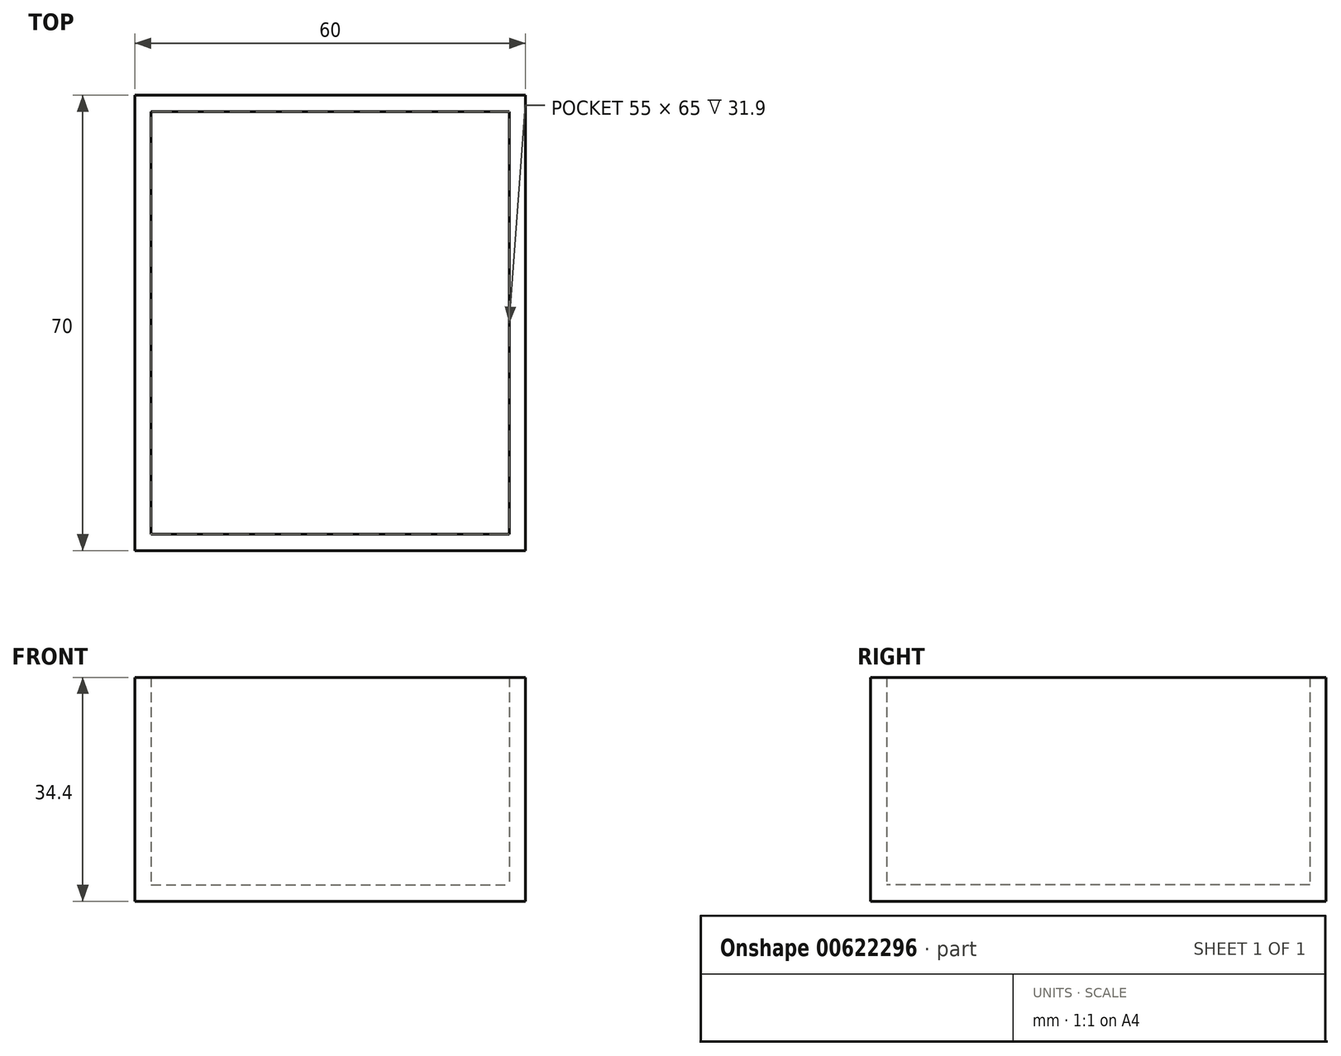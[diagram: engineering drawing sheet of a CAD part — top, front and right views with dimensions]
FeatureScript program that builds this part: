
annotation { "Feature Type Name" : "Feature", "Feature Type Description" : "" }
export const myFeature = defineFeature(function(context is Context, id is Id, definition is map)
    precondition{}
    {
        {
            var Q0;
            Q0=qCreatedBy(makeId("Top.planeOp"),FACE);
            var sketch = newSketch(context, id + "F0", { "sketchPlane" : qUnion([Q0])});
            skLineSegment(sketch, "E0.bottom", {"start": v(-30, 49.8) * mm, "end": v(30, 49.8) * mm});
            skLineSegment(sketch, "E0.top", {"start": v(-30, -20.2) * mm, "end": v(30, -20.2) * mm});
            skLineSegment(sketch, "E0.left", {"start": v(-30, 49.8) * mm, "end": v(-30, -20.2) * mm});
            skLineSegment(sketch, "E0.right", {"start": v(30, 49.8) * mm, "end": v(30, -20.2) * mm});
            skPoint(sketch, "E1", {"position": v(0, 49.8) * mm});
            skSolve(sketch);
        }
        {
            var Q0;
            Q0 = qSketchRegion(id + "F0", true);
            extrude(context, id + "F1", {"entities" : qUnion([Q0]), "depth" : 34.4 * mm, "offsetDistance" : 25 * mm});
        }
        {
            var Q0;
            Q0=makeQuery(id+"F1.opExtrude","CAP_FACE",FACE,{"disambiguationData":[OSD([sQuery(id+"F0.wireOp",EDGE,"E0.bottom"),sQuery(id+"F0.wireOp",EDGE,"E0.top"),sQuery(id+"F0.wireOp",EDGE,"E0.left"),sQuery(id+"F0.wireOp",EDGE,"E0.right")])],"isStart":false});
            shell(context, id + "F2", {"entities" : qUnion([Q0]), "thickness" : 2.5 * mm});
        }
    });
